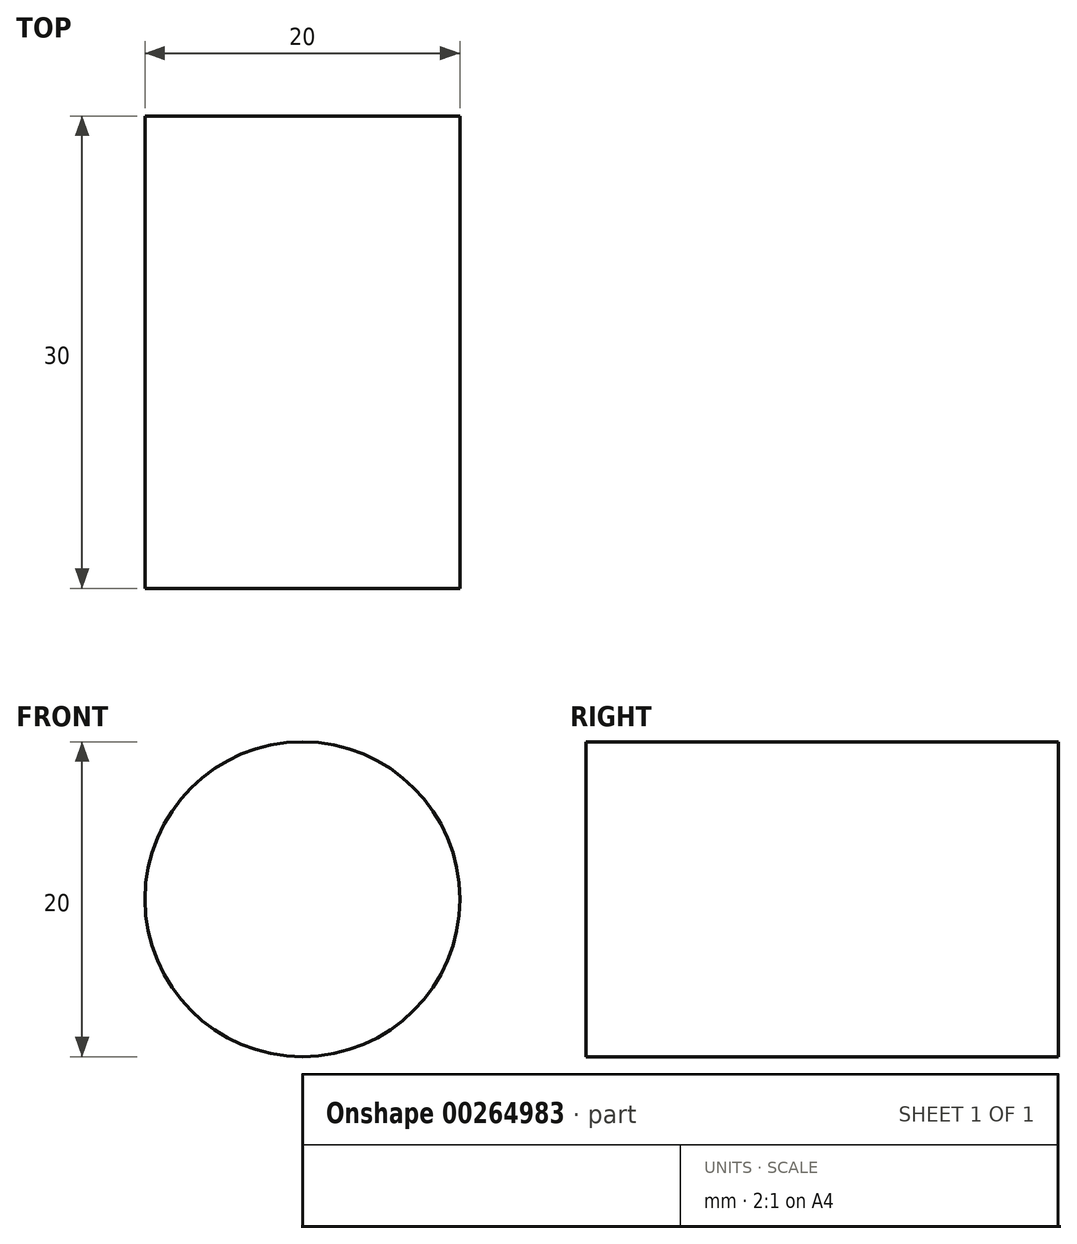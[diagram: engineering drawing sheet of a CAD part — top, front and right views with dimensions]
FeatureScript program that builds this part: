
annotation { "Feature Type Name" : "Feature", "Feature Type Description" : "" }
export const myFeature = defineFeature(function(context is Context, id is Id, definition is map)
    precondition{}
    {
        {
            var Q0;
            Q0=qCreatedBy(makeId("Front.planeOp"),FACE);
            var sketch = newSketch(context, id + "F0", { "sketchPlane" : qUnion([Q0])});
            skCircle(sketch, "E0", {"center": v(0, 0) * mm, "radius": 10 * mm});
            skSolve(sketch);
        }
        {
            var Q0;
            Q0 = qSketchRegion(id + "F0", true);
            extrude(context, id + "F1", {"entities" : qUnion([Q0]), "depth" : 30 * mm});
        }
    });
